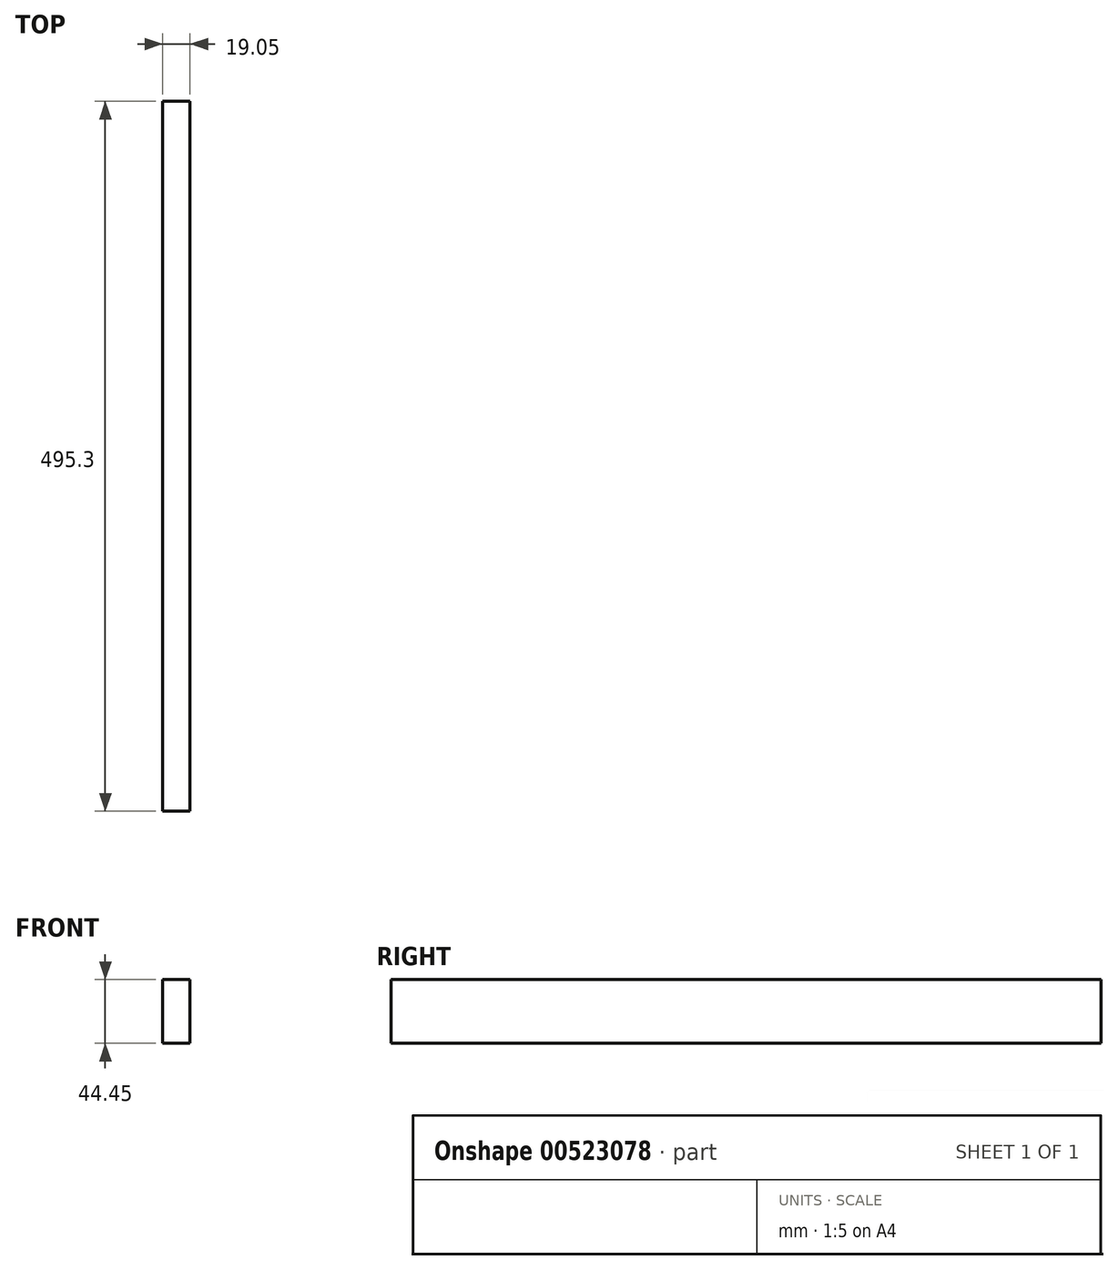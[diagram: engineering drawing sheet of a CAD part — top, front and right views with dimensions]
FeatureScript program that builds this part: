
annotation { "Feature Type Name" : "Feature", "Feature Type Description" : "" }
export const myFeature = defineFeature(function(context is Context, id is Id, definition is map)
    precondition{}
    {
        {
            var Q0;
            Q0=qCreatedBy(makeId("Front.planeOp"),FACE);
            var sketch = newSketch(context, id + "F0", { "sketchPlane" : qUnion([Q0])});
            skLineSegment(sketch, "E0.bottom", {"start": v(0, 0) * mm, "end": v(19.05, 0) * mm});
            skLineSegment(sketch, "E0.top", {"start": v(0, 44.45) * mm, "end": v(19.05, 44.45) * mm});
            skLineSegment(sketch, "E0.left", {"start": v(0, 0) * mm, "end": v(0, 44.45) * mm});
            skLineSegment(sketch, "E0.right", {"start": v(19.05, 0) * mm, "end": v(19.05, 44.45) * mm});
            skSolve(sketch);
        }
        {
            var Q0;
            Q0=qSketchRegion(id+"F0",true);
            extrude(context, id + "F1", {"entities" : qUnion([Q0]), "depth" : 495.3 * mm, "offsetDistance" : 25.4 * mm});
        }
    });
